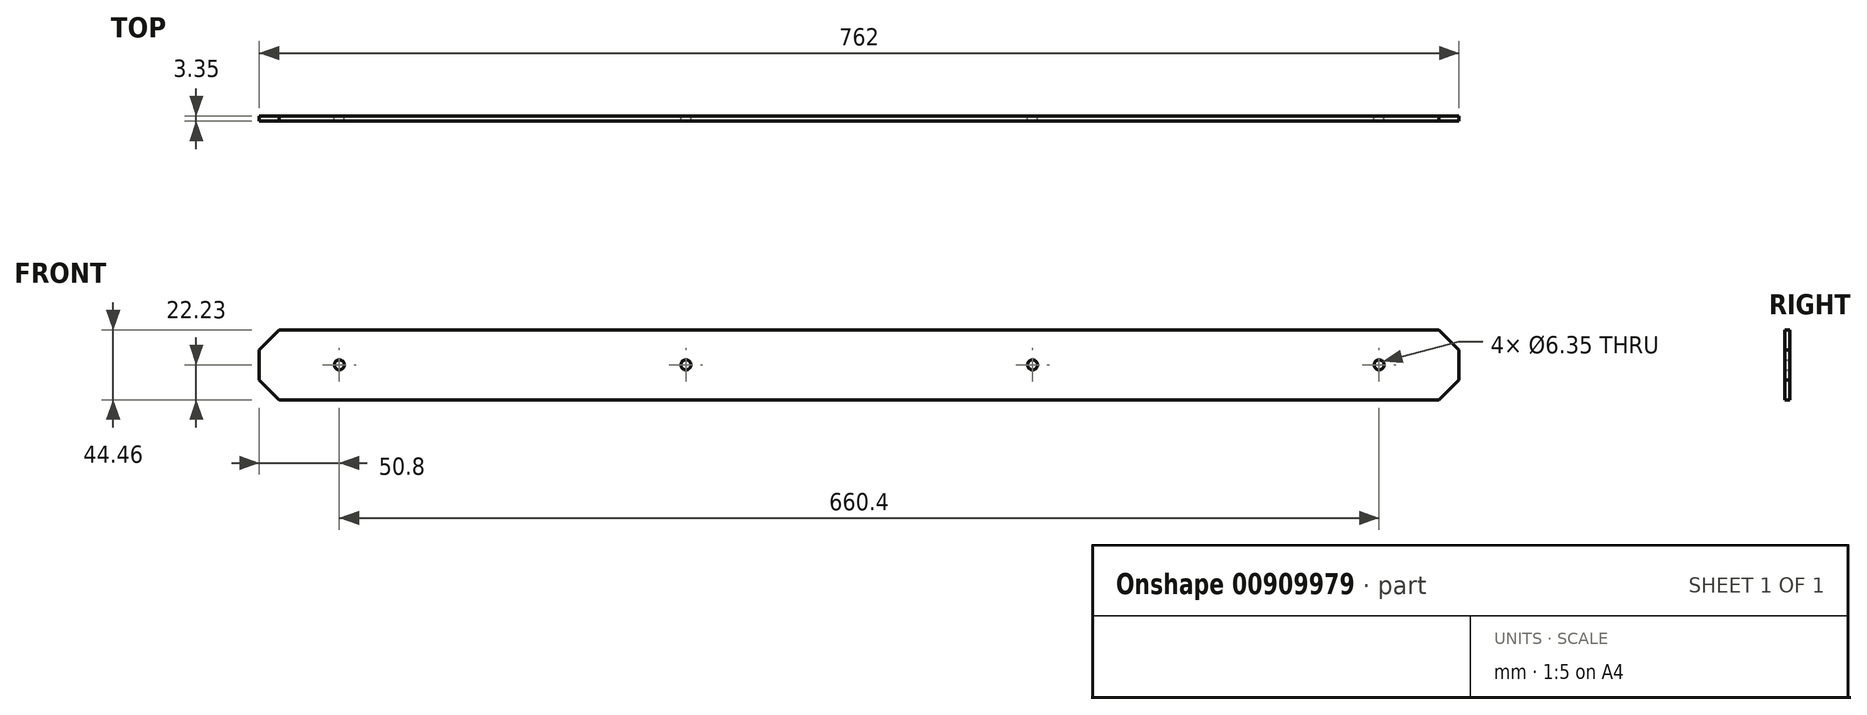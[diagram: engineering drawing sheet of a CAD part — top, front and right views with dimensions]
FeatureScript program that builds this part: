
annotation { "Feature Type Name" : "Feature", "Feature Type Description" : "" }
export const myFeature = defineFeature(function(context is Context, id is Id, definition is map)
    precondition{}
    {
        {
            var Q0;
            Q0=qCreatedBy(makeId("Front.planeOp"),FACE);
            var sketch = newSketch(context, id + "F0", { "sketchPlane" : qUnion([Q0])});
            skLineSegment(sketch, "E0.bottom", {"start": v(-381, 22.23) * mm, "end": v(381, 22.22) * mm});
            skLineSegment(sketch, "E0.top", {"start": v(-381, -22.23) * mm, "end": v(381, -22.22) * mm});
            skLineSegment(sketch, "E1", {"start": v(0, 22.23) * mm, "end": v(0, -22.23) * mm, "construction": true});
            skLineSegment(sketch, "E2", {"start": v(381, 22.22) * mm, "end": v(381, -22.22) * mm});
            skLineSegment(sketch, "E3", {"start": v(-381, 22.22) * mm, "end": v(-381, -22.22) * mm});
            skLineSegment(sketch, "E4", {"start": v(-381, 0) * mm, "end": v(-330.2, 0) * mm, "construction": true});
            skCircle(sketch, "E5", {"center": v(-330.2, 0) * mm, "radius": 3.17 * mm});
            skCircle(sketch, "E6", {"center": v(-110.07, 0) * mm, "radius": 3.17 * mm});
            skCircle(sketch, "E7", {"center": v(110.07, 0) * mm, "radius": 3.17 * mm});
            skCircle(sketch, "E8", {"center": v(330.2, 0) * mm, "radius": 3.17 * mm});
            skLineSegment(sketch, "E9", {"start": v(-330.2, 0) * mm, "end": v(-110.07, 0) * mm, "construction": true});
            skLineSegment(sketch, "E10", {"start": v(-110.07, 0) * mm, "end": v(110.07, 0) * mm, "construction": true});
            skLineSegment(sketch, "E11", {"start": v(110.07, 0) * mm, "end": v(330.2, 0) * mm, "construction": true});
            skLineSegment(sketch, "E12", {"start": v(330.2, 0) * mm, "end": v(381, 0) * mm, "construction": true});
            skSolve(sketch);
        }
        {
            var Q0;
            Q0=makeQuery(id+"F0.imprint","IMPRINT",FACE,{"disambiguationData":[TD([[makeQuery(id+"F0.imprint","IMPRINT",EDGE,{"derivedFrom":sQuery(id+"F0.wireOp",EDGE,"E0.bottom")}),-1.0]])]});
            extrude(context, id + "F1", {"entities" : qUnion([Q0]), "depth" : 3.35 * mm, "offsetDistance" : 25 * mm});
        }
        {
            var Q0;
            Q0=makeQuery(id+"F1.opExtrude","SWEPT_EDGE",EDGE,{"disambiguationData":[OSD([sQuery(id+"F0.wireOp",EDGE,"E0.top"),sQuery(id+"F0.wireOp",EDGE,"E2")])]});
            var Q1;
            Q1=makeQuery(id+"F1.opExtrude","SWEPT_EDGE",EDGE,{"disambiguationData":[OSD([sQuery(id+"F0.wireOp",EDGE,"E0.bottom"),sQuery(id+"F0.wireOp",EDGE,"E2")])]});
            var Q2;
            Q2=makeQuery(id+"F1.opExtrude","SWEPT_EDGE",EDGE,{"disambiguationData":[OSD([sQuery(id+"F0.wireOp",EDGE,"E0.bottom"),sQuery(id+"F0.wireOp",EDGE,"E3")])]});
            var Q3;
            Q3=makeQuery(id+"F1.opExtrude","SWEPT_EDGE",EDGE,{"disambiguationData":[OSD([sQuery(id+"F0.wireOp",EDGE,"E0.top"),sQuery(id+"F0.wireOp",EDGE,"E3")])]});
            chamfer(context, id + "F2", {"entities" : qUnion([Q0, Q1, Q2, Q3]), "width" : 12.7 * mm, "tangentPropagation" : true});
        }
    });
